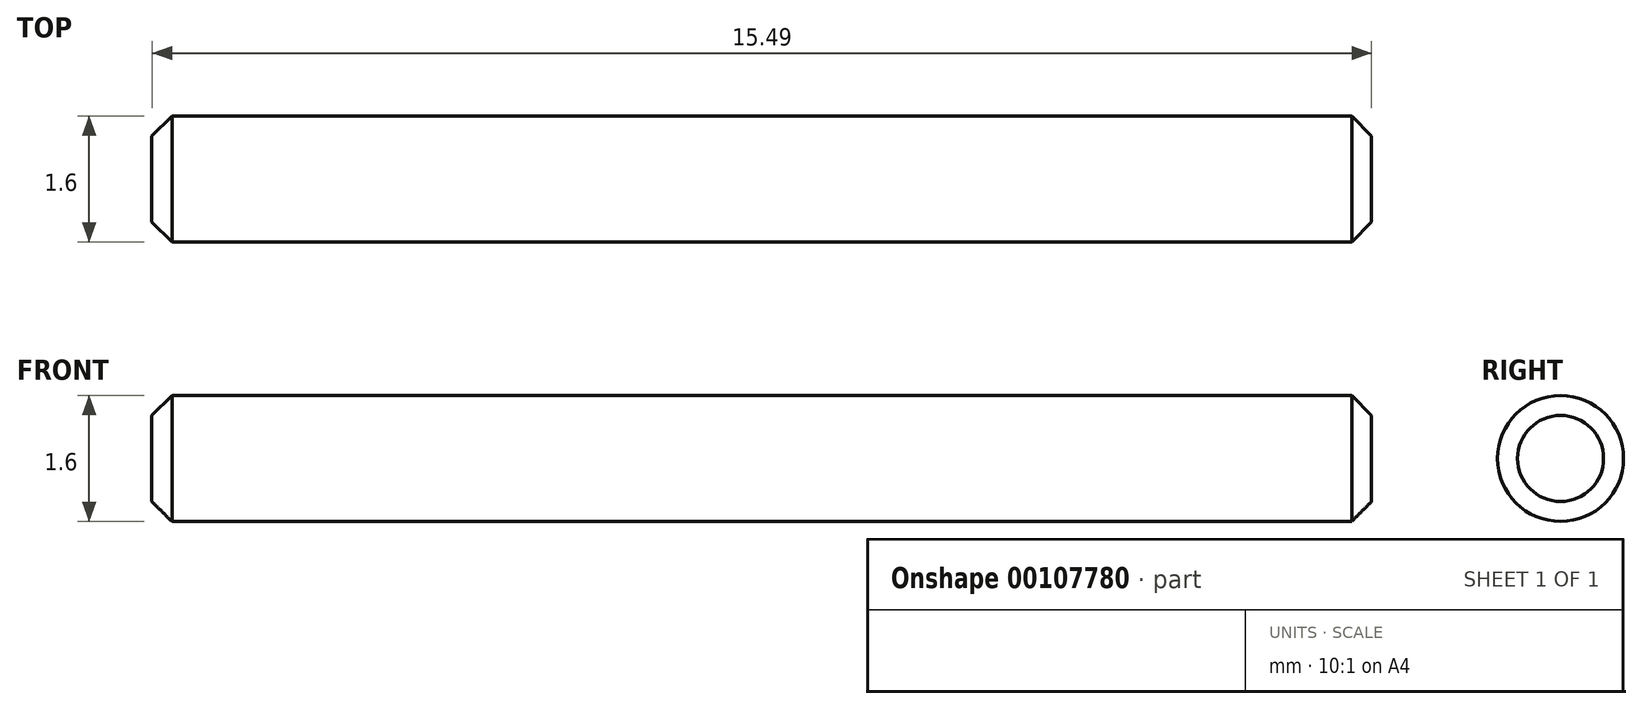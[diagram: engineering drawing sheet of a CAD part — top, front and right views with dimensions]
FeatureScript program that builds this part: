
annotation { "Feature Type Name" : "Feature", "Feature Type Description" : "" }
export const myFeature = defineFeature(function(context is Context, id is Id, definition is map)
    precondition{}
    {
        {
            var Q0;
            Q0=qCreatedBy(makeId("Right.planeOp"),FACE);
            var sketch = newSketch(context, id + "F0", { "sketchPlane" : qUnion([Q0])});
            skCircle(sketch, "E0", {"center": v(0, 0) * mm, "radius": 0.8 * mm});
            skSolve(sketch);
        }
        {
            var Q0;
            Q0=makeQuery(id+"F0.imprint","IMPRINT",FACE,{"disambiguationData":[TD([[makeQuery(id+"F0.imprint","IMPRINT",EDGE,{"derivedFrom":sQuery(id+"F0.wireOp",EDGE,"E0")}),1.0]])]});
            extrude(context, id + "F1", {"entities" : qUnion([Q0]), "oppositeDirection" : true, "depth" : 15.5 * mm});
        }
        {
            var Q0;
            Q0=makeQuery(id+"F1.opExtrude","CAP_EDGE",EDGE,{"disambiguationData":[OSD([sQuery(id+"F0.wireOp",EDGE,"E0")])],"isStart":false});
            var Q1;
            Q1=makeQuery(id+"F1.opExtrude","CAP_EDGE",EDGE,{"disambiguationData":[OSD([sQuery(id+"F0.wireOp",EDGE,"E0")])],"isStart":true});
            chamfer(context, id + "F2", {"entities" : qUnion([Q0, Q1]), "chamferType" : ChamferType.OFFSET_ANGLE, "width" : 0.25 * mm, "oppositeDirection" : false, "angle" : 45 * degree, "tangentPropagation" : true});
        }
    });
